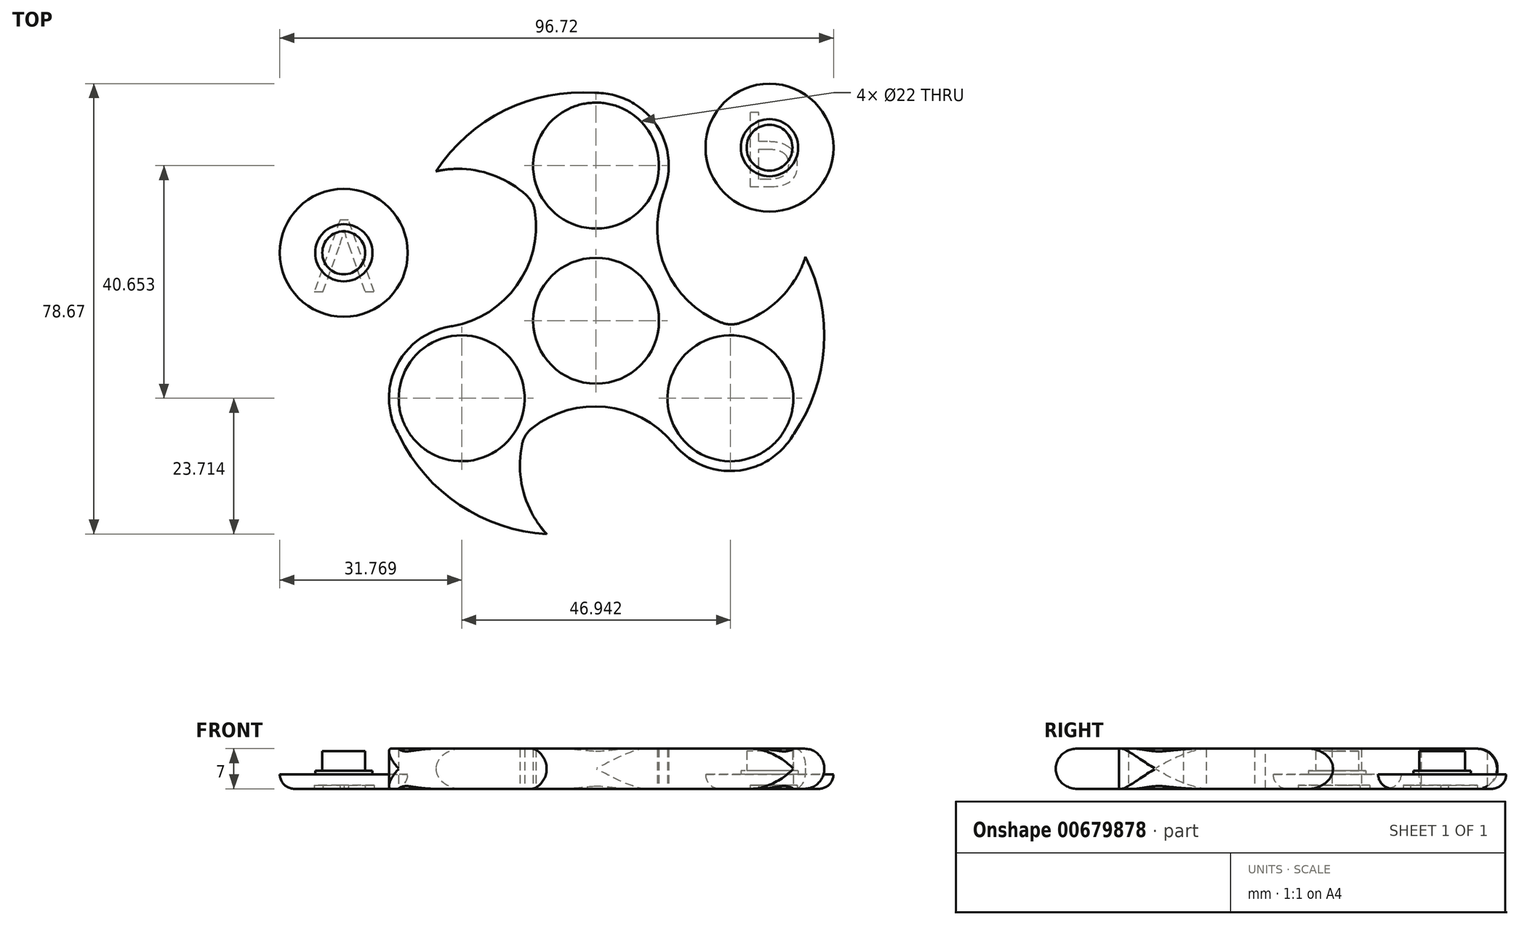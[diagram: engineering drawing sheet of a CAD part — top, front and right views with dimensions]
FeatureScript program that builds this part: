
annotation { "Feature Type Name" : "Feature", "Feature Type Description" : "" }
export const myFeature = defineFeature(function(context is Context, id is Id, definition is map)
    precondition{}
    {
        {
            var Q0;
            Q0=qCreatedBy(makeId("Top.planeOp"),FACE);
            var sketch = newSketch(context, id + "F0", { "sketchPlane" : qUnion([Q0])});
            skCircle(sketch, "E0", {"center": v(0, 40.4) * mm, "radius": 11 * mm});
            skCircle(sketch, "E1.1.0", {"center": v(-23.47, -0.25) * mm, "radius": 11 * mm});
            skCircle(sketch, "E1.2.0", {"center": v(23.47, -0.25) * mm, "radius": 11 * mm});
            skPoint(sketch, "E1.center", {"position": v(0, 13.3) * mm});
            skCircle(sketch, "E2", {"center": v(0, 13.3) * mm, "radius": 11 * mm});
            skCircle(sketch, "E3", {"center": v(0, 40.4) * mm, "radius": 12.7 * mm});
            skCircle(sketch, "E4.1.0", {"center": v(-23.47, -0.25) * mm, "radius": 12.7 * mm});
            skCircle(sketch, "E4.2.0", {"center": v(23.47, -0.25) * mm, "radius": 12.7 * mm});
            skArc(sketch, "E5", {"start": v(11.95, 36.1) * mm, "mid": v(12.48, 21.73) * mm, "end": v(23.47, 12.45) * mm});
            skArc(sketch, "E6.1.0", {"start": v(-25.72, 12.25) * mm, "mid": v(-13.54, 19.9) * mm, "end": v(-11, 34.06) * mm});
            skArc(sketch, "E6.2.0", {"start": v(13.77, -8.44) * mm, "mid": v(1.06, -1.72) * mm, "end": v(-12.47, -6.6) * mm});
            skArc(sketch, "E7", {"start": v(-11, 34.06) * mm, "mid": v(-18.76, 39) * mm, "end": v(-27.95, 39.41) * mm});
            skArc(sketch, "E8.1.0", {"start": v(-12.47, -6.6) * mm, "mid": v(-12.88, -15.8) * mm, "end": v(-8.63, -23.96) * mm});
            skArc(sketch, "E8.2.0", {"start": v(23.47, 12.45) * mm, "mid": v(31.64, 16.7) * mm, "end": v(36.59, 24.46) * mm});
            skArc(sketch, "E9", {"start": v(-35.8, -3.33) * mm, "mid": v(-25.37, -17.8) * mm, "end": v(-8.63, -23.96) * mm});
            skArc(sketch, "E10.1.0", {"start": v(32.3, -9.37) * mm, "mid": v(39.62, 6.89) * mm, "end": v(36.59, 24.46) * mm});
            skArc(sketch, "E10.2.0", {"start": v(3.49, 52.62) * mm, "mid": v(-14.25, 50.82) * mm, "end": v(-27.95, 39.41) * mm});
            skSolve(sketch);
        }
        {
            var Q0;
            Q0=qSketchRegion(id+"F0",true);
            extrude(context, id + "F1", {"entities" : qUnion([Q0]), "depth" : 7 * mm, "offsetDistance" : 25.4 * mm});
        }
        {
            var Q0;
            Q0=makeQuery(id+"F1.opExtrude","SWEPT_EDGE",EDGE,{"disambiguationData":[OSD([sQuery(id+"F0.wireOp",EDGE,"E3"),sQuery(id+"F0.wireOp",EDGE,"E10.2.0")])]});
            var Q1;
            Q1=makeQuery(id+"F1.opExtrude","SWEPT_EDGE",EDGE,{"disambiguationData":[OSD([sQuery(id+"F0.wireOp",EDGE,"E4.2.0"),sQuery(id+"F0.wireOp",EDGE,"E10.1.0")])]});
            var Q2;
            Q2=makeQuery(id+"F1.opExtrude","SWEPT_EDGE",EDGE,{"disambiguationData":[OSD([sQuery(id+"F0.wireOp",EDGE,"E4.1.0"),sQuery(id+"F0.wireOp",EDGE,"E6.2.0"),sQuery(id+"F0.wireOp",EDGE,"E8.1.0")])]});
            var Q3;
            Q3=makeQuery(id+"F1.opExtrude","SWEPT_EDGE",EDGE,{"disambiguationData":[OSD([sQuery(id+"F0.wireOp",EDGE,"E4.2.0"),sQuery(id+"F0.wireOp",EDGE,"E5"),sQuery(id+"F0.wireOp",EDGE,"E8.2.0")])]});
            var Q4;
            Q4=makeQuery(id+"F1.opExtrude","SWEPT_EDGE",EDGE,{"disambiguationData":[OSD([sQuery(id+"F0.wireOp",EDGE,"E3"),sQuery(id+"F0.wireOp",EDGE,"E5")])]});
            var Q5;
            Q5=makeQuery(id+"F1.opExtrude","SWEPT_EDGE",EDGE,{"disambiguationData":[OSD([sQuery(id+"F0.wireOp",EDGE,"E3"),sQuery(id+"F0.wireOp",EDGE,"E6.1.0"),sQuery(id+"F0.wireOp",EDGE,"E7")])]});
            var Q6;
            Q6=makeQuery(id+"F1.opExtrude","SWEPT_EDGE",EDGE,{"disambiguationData":[OSD([sQuery(id+"F0.wireOp",EDGE,"E4.1.0"),sQuery(id+"F0.wireOp",EDGE,"E9")])]});
            var Q7;
            Q7=makeQuery(id+"F1.opExtrude","SWEPT_EDGE",EDGE,{"disambiguationData":[OSD([sQuery(id+"F0.wireOp",EDGE,"E4.2.0"),sQuery(id+"F0.wireOp",EDGE,"E6.2.0")])]});
            var Q8;
            Q8=makeQuery(id+"F1.opExtrude","SWEPT_EDGE",EDGE,{"disambiguationData":[OSD([sQuery(id+"F0.wireOp",EDGE,"E4.1.0"),sQuery(id+"F0.wireOp",EDGE,"E6.1.0")])]});
            fillet(context, id + "F2", {"entities" : qUnion([Q0, Q1, Q2, Q3, Q4, Q5, Q6, Q7, Q8]), "radius" : 4.83 * mm, "tangentPropagation" : true, "rho" : 0.5, "crossSection" : FilletCrossSection.CONIC, "allowEdgeOverflow" : false});
        }
        {
            var Q0;
            Q0=makeQuery(id+"F1.opExtrude","CAP_EDGE",EDGE,{"disambiguationData":[OSD([sQuery(id+"F0.wireOp",EDGE,"E10.1.0")])],"isStart":false});
            var Q1;
            Q1=makeQuery(id+"F1.opExtrude","CAP_EDGE",EDGE,{"disambiguationData":[OSD([sQuery(id+"F0.wireOp",EDGE,"E9")])],"isStart":false});
            var Q2;
            Q2=makeQuery(id+"F1.opExtrude","CAP_EDGE",EDGE,{"disambiguationData":[OSD([sQuery(id+"F0.wireOp",EDGE,"E10.2.0")])],"isStart":false});
            var Q3;
            Q3=makeQuery(id+"F1.opExtrude","CAP_EDGE",EDGE,{"disambiguationData":[OSD([sQuery(id+"F0.wireOp",EDGE,"E9")])],"isStart":true});
            var Q4;
            Q4=makeQuery(id+"F1.opExtrude","CAP_EDGE",EDGE,{"disambiguationData":[OSD([sQuery(id+"F0.wireOp",EDGE,"E10.1.0")])],"isStart":true});
            var Q5;
            Q5=makeQuery(id+"F1.opExtrude","CAP_EDGE",EDGE,{"disambiguationData":[OSD([sQuery(id+"F0.wireOp",EDGE,"E10.2.0")])],"isStart":true});
            fillet(context, id + "F3", {"entities" : qUnion([Q0, Q1, Q2, Q3, Q4, Q5]), "radius" : 3.43 * mm, "tangentPropagation" : true, "allowEdgeOverflow" : false});
        }
        {
            var Q0;
            Q0=qCreatedBy(makeId("Top.planeOp"),FACE);
            var sketch = newSketch(context, id + "F4", { "sketchPlane" : qUnion([Q0])});
            skCircle(sketch, "E11", {"center": v(30.3, 43.54) * mm, "radius": 11.18 * mm});
            skCircle(sketch, "E12", {"center": v(-44.06, 25.17) * mm, "radius": 11.18 * mm});
            skSolve(sketch);
        }
        {
            var Q0;
            Q0=makeQuery(id+"F4.imprint","IMPRINT",FACE,{"disambiguationData":[TD([[makeQuery(id+"F4.imprint","IMPRINT",EDGE,{"derivedFrom":sQuery(id+"F4.wireOp",EDGE,"E12")}),1.0]])]});
            var Q1;
            Q1=makeQuery(id+"F4.imprint","IMPRINT",FACE,{"disambiguationData":[TD([[makeQuery(id+"F4.imprint","IMPRINT",EDGE,{"derivedFrom":sQuery(id+"F4.wireOp",EDGE,"E11")}),1.0]])]});
            extrude(context, id + "F5", {"entities" : qUnion([Q0, Q1]), "depth" : 2.54 * mm, "offsetDistance" : 25.4 * mm});
        }
        {
            var Q0;
            Q0=makeQuery(id+"F5.opExtrude","CAP_EDGE",EDGE,{"disambiguationData":[OSD([sQuery(id+"F4.wireOp",EDGE,"E12")])],"isStart":true});
            var Q1;
            Q1=makeQuery(id+"F5.opExtrude","CAP_EDGE",EDGE,{"disambiguationData":[OSD([sQuery(id+"F4.wireOp",EDGE,"E11")])],"isStart":true});
            fillet(context, id + "F6", {"entities" : qUnion([Q0, Q1]), "radius" : 2.54 * mm, "tangentPropagation" : true, "allowEdgeOverflow" : false});
        }
        {
            var Q0;
            Q0=makeQuery(id+"F5.opExtrude","CAP_FACE",FACE,{"disambiguationData":[OSD([sQuery(id+"F4.wireOp",EDGE,"E12")])],"isStart":true});
            var sketch = newSketch(context, id + "F7", { "sketchPlane" : qUnion([Q0])});
            skText(sketch, "E13", { "text": "V", "fontName": "OpenSans-Regular.ttf"});
            const initialGuessF7  = {"E13": [-0.04923, -0.03092, 1, 0, 0.01267]};
            skSetInitialGuess(sketch, initialGuessF7);
            skSolve(sketch);
        }
        {
            var Q0;
            Q0=makeQuery(id+"F5.opExtrude","CAP_FACE",FACE,{"disambiguationData":[OSD([sQuery(id+"F4.wireOp",EDGE,"E11")])],"isStart":true});
            var sketch = newSketch(context, id + "F8", { "sketchPlane" : qUnion([Q0])});
            skText(sketch, "E14", { "text": "P", "fontName": "OpenSans-Regular.ttf"});
            const initialGuessF8  = {"E14": [0.02515, -0.0497, 1, 0, 0.0131]};
            skSetInitialGuess(sketch, initialGuessF8);
            skSolve(sketch);
        }
        {
            var Q0;
            Q0 = qSketchRegion(id + "F7", true);
            extrude(context, id + "F9", {"entities" : qUnion([Q0]), "operationType" : NewBodyOperationType.REMOVE, "oppositeDirection" : true, "depth" : 0.64 * mm, "offsetDistance" : 25.4 * mm});
        }
        {
            var Q0;
            Q0 = qSketchRegion(id + "F8", true);
            extrude(context, id + "F10", {"entities" : qUnion([Q0]), "operationType" : NewBodyOperationType.REMOVE, "oppositeDirection" : true, "depth" : 0.64 * mm, "offsetDistance" : 25.4 * mm});
        }
        {
            var Q0;
            Q0=makeQuery(id+"F5.opExtrude","CAP_FACE",FACE,{"disambiguationData":[OSD([sQuery(id+"F4.wireOp",EDGE,"E12")])],"isStart":false});
            var sketch = newSketch(context, id + "F11", { "sketchPlane" : qUnion([Q0])});
            skCircle(sketch, "E15", {"center": v(-44.06, 25.17) * mm, "radius": 5 * mm});
            skSolve(sketch);
        }
        {
            var Q0;
            Q0=makeQuery(id+"F11.imprint","IMPRINT",FACE,{"disambiguationData":[TD([[makeQuery(id+"F11.imprint","IMPRINT",EDGE,{"derivedFrom":sQuery(id+"F11.wireOp",EDGE,"E15")}),1.0]])]});
            extrude(context, id + "F12", {"entities" : qUnion([Q0]), "operationType" : NewBodyOperationType.ADD, "depth" : 0.64 * mm, "offsetDistance" : 25.4 * mm});
        }
        {
            var Q0;
            Q0=makeQuery(id+"F12.opExtrude","CAP_FACE",FACE,{"disambiguationData":[OSD([sQuery(id+"F11.wireOp",EDGE,"E15")])],"isStart":false});
            var sketch = newSketch(context, id + "F13", { "sketchPlane" : qUnion([Q0])});
            skCircle(sketch, "E16", {"center": v(-44.06, 25.17) * mm, "radius": 3.75 * mm});
            skSolve(sketch);
        }
        {
            var Q0;
            Q0=makeQuery(id+"F13.imprint","IMPRINT",FACE,{"disambiguationData":[TD([[makeQuery(id+"F13.imprint","IMPRINT",EDGE,{"derivedFrom":sQuery(id+"F13.wireOp",EDGE,"E16")}),1.0]])]});
            extrude(context, id + "F14", {"entities" : qUnion([Q0]), "operationType" : NewBodyOperationType.ADD, "depth" : 3.4 * mm, "offsetDistance" : 25.4 * mm});
        }
        {
            var Q0;
            Q0=makeQuery(id+"F5.opExtrude","CAP_FACE",FACE,{"disambiguationData":[OSD([sQuery(id+"F4.wireOp",EDGE,"E11")])],"isStart":false});
            var sketch = newSketch(context, id + "F15", { "sketchPlane" : qUnion([Q0])});
            skCircle(sketch, "E17", {"center": v(30.3, 43.54) * mm, "radius": 5 * mm});
            skSolve(sketch);
        }
        {
            var Q0;
            Q0=makeQuery(id+"F15.imprint","IMPRINT",FACE,{"disambiguationData":[TD([[makeQuery(id+"F15.imprint","IMPRINT",EDGE,{"derivedFrom":sQuery(id+"F15.wireOp",EDGE,"E17")}),1.0]])]});
            extrude(context, id + "F16", {"entities" : qUnion([Q0]), "operationType" : NewBodyOperationType.ADD, "depth" : 0.64 * mm, "offsetDistance" : 25.4 * mm});
        }
        {
            var Q0;
            Q0=makeQuery(id+"F16.opExtrude","CAP_FACE",FACE,{"disambiguationData":[OSD([sQuery(id+"F15.wireOp",EDGE,"E17")])],"isStart":false});
            var sketch = newSketch(context, id + "F17", { "sketchPlane" : qUnion([Q0])});
            skCircle(sketch, "E18", {"center": v(30.3, 43.54) * mm, "radius": 4 * mm});
            skSolve(sketch);
        }
        {
            var Q0;
            Q0=makeQuery(id+"F17.imprint","IMPRINT",FACE,{"disambiguationData":[TD([[makeQuery(id+"F17.imprint","IMPRINT",EDGE,{"derivedFrom":sQuery(id+"F17.wireOp",EDGE,"E18")}),1.0]])]});
            extrude(context, id + "F18", {"entities" : qUnion([Q0]), "operationType" : NewBodyOperationType.ADD, "depth" : 3.4 * mm, "offsetDistance" : 25.4 * mm});
        }
    });
